# Revit family: Hinge_TCA1L2S3BT_TruClose_DD-Technologies-Pair
name_source: partatom
category: Specialty Equipment
units: mm (PartAtom-declared; Revit-internal decimal feet)

## family parameters
Always vertical = Yes
Cut with Voids When Loaded = No
Enable Cutting in Views = No
Maintain Annotation Orientation = No
Part Type = Normal
Room Calculation Point = No
Round Connector Dimension = Use Diameter
Shared = No
Work Plane-Based = Yes

## types (1)
- TCA1L2S3BT - Adjustable self-closing hinge for pools & Safety gates
    Assembly Code = G2060.20 Fences and Gates
    Catalog Page = https://us.ddtech.com
    Colors = Black
    Default Elevation = 0' - 1 7/8"
    Description = Adjustable, self-closing hinge for pool & safety gates, 2 legs, black, black trim, for metal gates
    Fence Material = Metal
    Fixed Gate Gap = 13/16" (21mm)
    Gate Hinge Length = 1 1/16" (27mm)
    Gate Material = Metal
    Hinge Material = Reinforced Polymer
    Keynote = 32 31 00 Fence & Gates
    Manufacturer = D&D Technologies
    Maximal Self-Closing Gate Weight*  (per pair of hinge) = 66 lb (30kg)
    Model = TCA1L2S3BT
    Post Hinge Length = 1 1/16" (27mm)
    Product Name = TruClose® Regular
    Product Webpage with product image = https://us.ddtech.com
    Side Legs = 2 Legs
    Specification = https://us.ddtech.com
    Type = Adjustable self-closing hinge
    URL = https://ddtech.com

## geometry (parser evidence)
native form markers: Sweep x15
no freeform markers — native parametric forms only
